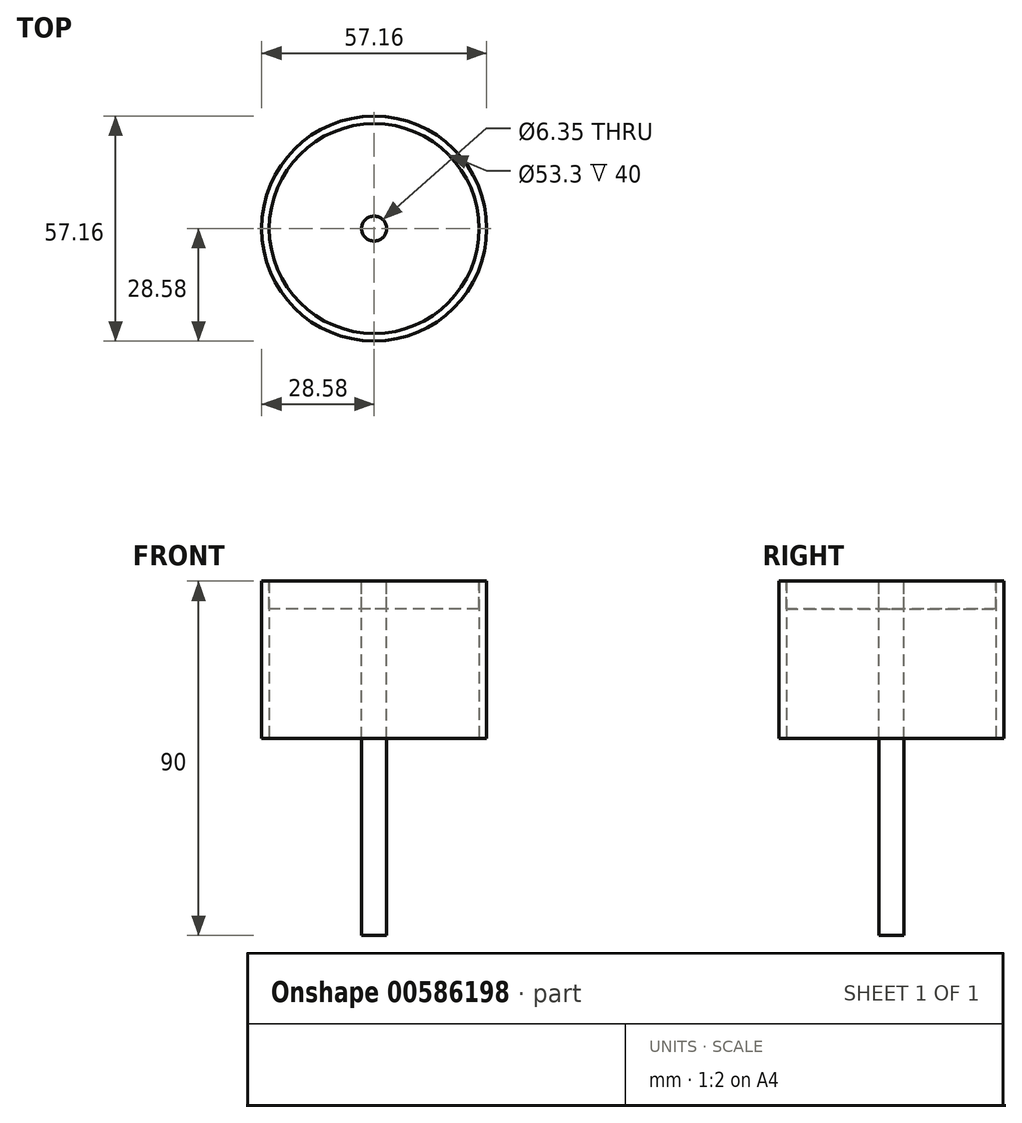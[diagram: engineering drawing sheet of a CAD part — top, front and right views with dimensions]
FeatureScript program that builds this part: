
annotation { "Feature Type Name" : "Feature", "Feature Type Description" : "" }
export const myFeature = defineFeature(function(context is Context, id is Id, definition is map)
    precondition{}
    {
        {
            var Q0;
            Q0=qCreatedBy(makeId("Top.planeOp"),FACE);
            var sketch = newSketch(context, id + "F0", { "sketchPlane" : qUnion([Q0])});
            skCircle(sketch, "E0", {"center": v(0, 0) * mm, "radius": 28.57 * mm});
            skCircle(sketch, "E1", {"center": v(0, 0) * mm, "radius": 26.65 * mm});
            skSolve(sketch);
        }
        {
            var Q0;
            Q0=makeQuery(id+"F0.imprint","IMPRINT",FACE,{"disambiguationData":[TD([[makeQuery(id+"F0.imprint","IMPRINT",EDGE,{"derivedFrom":sQuery(id+"F0.wireOp",EDGE,"E0")}),1.0]])]});
            extrude(context, id + "F1", {"entities" : qUnion([Q0]), "depth" : 40 * mm, "offsetDistance" : 25 * mm});
        }
        {
            var Q0;
            Q0=makeQuery(id+"F1.opExtrude","CAP_FACE",FACE,{"disambiguationData":[OSD([sQuery(id+"F0.wireOp",EDGE,"E0"),sQuery(id+"F0.wireOp",EDGE,"E1")])],"isStart":false});
            var sketch = newSketch(context, id + "F2", { "sketchPlane" : qUnion([Q0])});
            skCircle(sketch, "E2", {"center": v(0, 0) * mm, "radius": 28.6 * mm});
            skLineSegment(sketch, "E3", {"start": v(0, 0) * mm, "end": v(-28.57, 0) * mm, "construction": true});
            skCircle(sketch, "E4", {"center": v(0, 0) * mm, "radius": 28.57 * mm});
            skCircle(sketch, "E5", {"center": v(0, 0) * mm, "radius": 3.17 * mm});
            skSolve(sketch);
        }
        {
            var Q0;
            Q0=makeQuery(id+"F2.imprint","IMPRINT",FACE,{"disambiguationData":[TD([[makeQuery(id+"F2.imprint","IMPRINT",EDGE,{"derivedFrom":sQuery(id+"F2.wireOp",EDGE,"E5")}),-1.0]])]});
            extrude(context, id + "F3", {"entities" : qUnion([Q0]), "oppositeDirection" : true, "depth" : 7 * mm, "offsetDistance" : 25 * mm});
        }
        {
            var Q0;
            Q0=makeQuery(id+"F3.opExtrude","CAP_FACE",FACE,{"disambiguationData":[OSD([sQuery(id+"F0.wireOp",EDGE,"E1"),sQuery(id+"F2.wireOp",EDGE,"E5")])],"isStart":true});
            var sketch = newSketch(context, id + "F4", { "sketchPlane" : qUnion([Q0])});
            skLineSegment(sketch, "E6", {"start": v(0, 0) * mm, "end": v(-3.17, 0) * mm, "construction": true});
            skCircle(sketch, "E7", {"center": v(0, 0) * mm, "radius": 3.17 * mm});
            skSolve(sketch);
        }
        {
            var Q0;
            Q0 = qSketchRegion(id + "F4", true);
            extrude(context, id + "F5", {"entities" : qUnion([Q0]), "oppositeDirection" : true, "depth" : 90 * mm, "offsetDistance" : 25 * mm});
        }
    });
